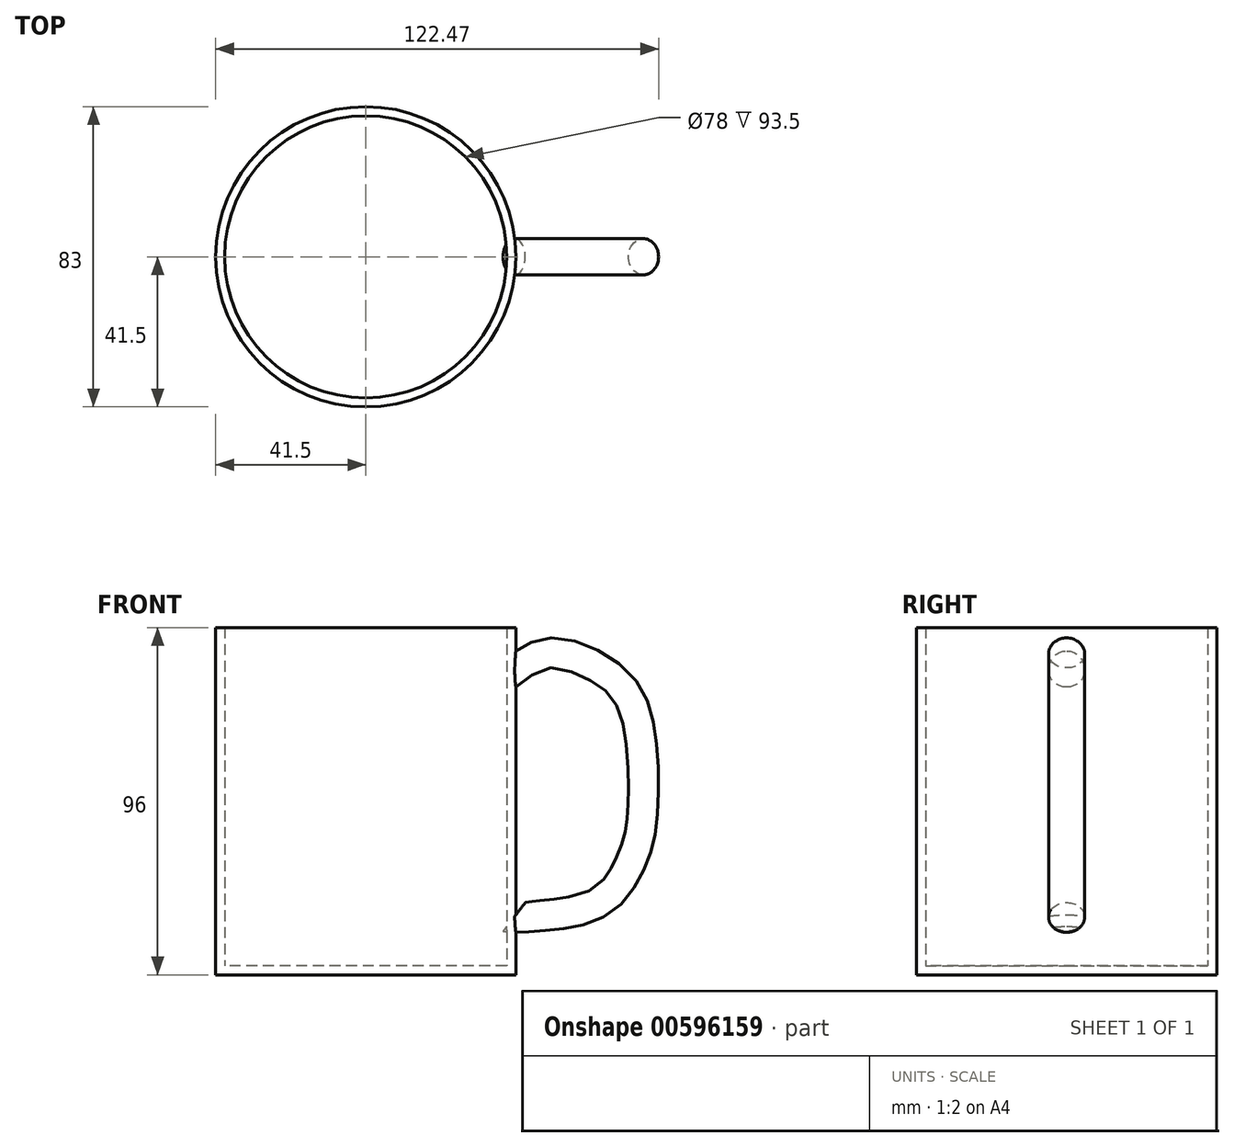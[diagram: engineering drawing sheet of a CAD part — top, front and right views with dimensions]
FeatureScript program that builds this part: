
annotation { "Feature Type Name" : "Feature", "Feature Type Description" : "" }
export const myFeature = defineFeature(function(context is Context, id is Id, definition is map)
    precondition{}
    {
        {
            var Q0;
            Q0=qCreatedBy(makeId("Top.planeOp"),FACE);
            var sketch = newSketch(context, id + "F0", { "sketchPlane" : qUnion([Q0])});
            skCircle(sketch, "E0", {"center": v(0, 0) * mm, "radius": 41.5 * mm});
            skSolve(sketch);
        }
        {
            var Q0;
            Q0 = qSketchRegion(id + "F0", true);
            extrude(context, id + "F1", {"entities" : qUnion([Q0]), "depth" : 96 * mm, "offsetDistance" : 25 * mm});
        }
        {
            var Q0;
            Q0=qCreatedBy(makeId("Right.planeOp"),FACE);
            cPlane(context, id + "F2", {"entities" : qUnion([Q0]), "cplaneType" : CPlaneType.OFFSET, "offset" : 41.3 * mm, "width" : 150 * mm, "height" : 150 * mm});
        }
        {
            var Q0;
            Q0=qCreatedBy(id+"F2.planeOp",FACE);
            var sketch = newSketch(context, id + "F3", { "sketchPlane" : qUnion([Q0])});
            skCircle(sketch, "E1", {"center": v(0, 84.4) * mm, "radius": 5 * mm});
            skSolve(sketch);
        }
        {
            var Q0;
            Q0=makeQuery(id+"F1.opExtrude","CAP_FACE",FACE,{"disambiguationData":[OSD([sQuery(id+"F0.wireOp",EDGE,"E0")])],"isStart":false});
            shell(context, id + "F4", {"entities" : qUnion([Q0]), "thickness" : 2.5 * mm});
        }
        {
            var Q0;
            Q0=qCreatedBy(makeId("Front.planeOp"),FACE);
            var sketch = newSketch(context, id + "F5", { "sketchPlane" : qUnion([Q0])});
            skFitSpline(sketch, "E2", {"points": [v(41.03, 84.31) * mm, v(51.53, 88.81) * mm, v(69.1, 81.31) * mm, v(75.74, 67.17) * mm, v(76.6, 45.32) * mm, v(73.81, 32.46) * mm, v(65.67, 20.9) * mm, v(53.03, 16.82) * mm, v(43.82, 15.96) * mm, v(41.01, 15.96) * mm], "startDerivative": vector(92.58, 60.84) * mm, "endDerivative": vector(-54.45, 4.27) * mm});
            skSolve(sketch);
        }
        {
            var Q0;
            Q0=makeQuery(id+"F3.imprint","IMPRINT",FACE,{"disambiguationData":[TD([[makeQuery(id+"F3.imprint","IMPRINT",EDGE,{"derivedFrom":sQuery(id+"F3.wireOp",EDGE,"E1")}),1.0]])]});
            var Q1;
            Q1=sQuery(id+"F5.wireOp",EDGE,"E2");
            sweep(context, id + "F6", {"operationType" : NewBodyOperationType.ADD, "profiles" : qUnion([Q0]), "path" : qUnion([Q1])});
        }
    });
